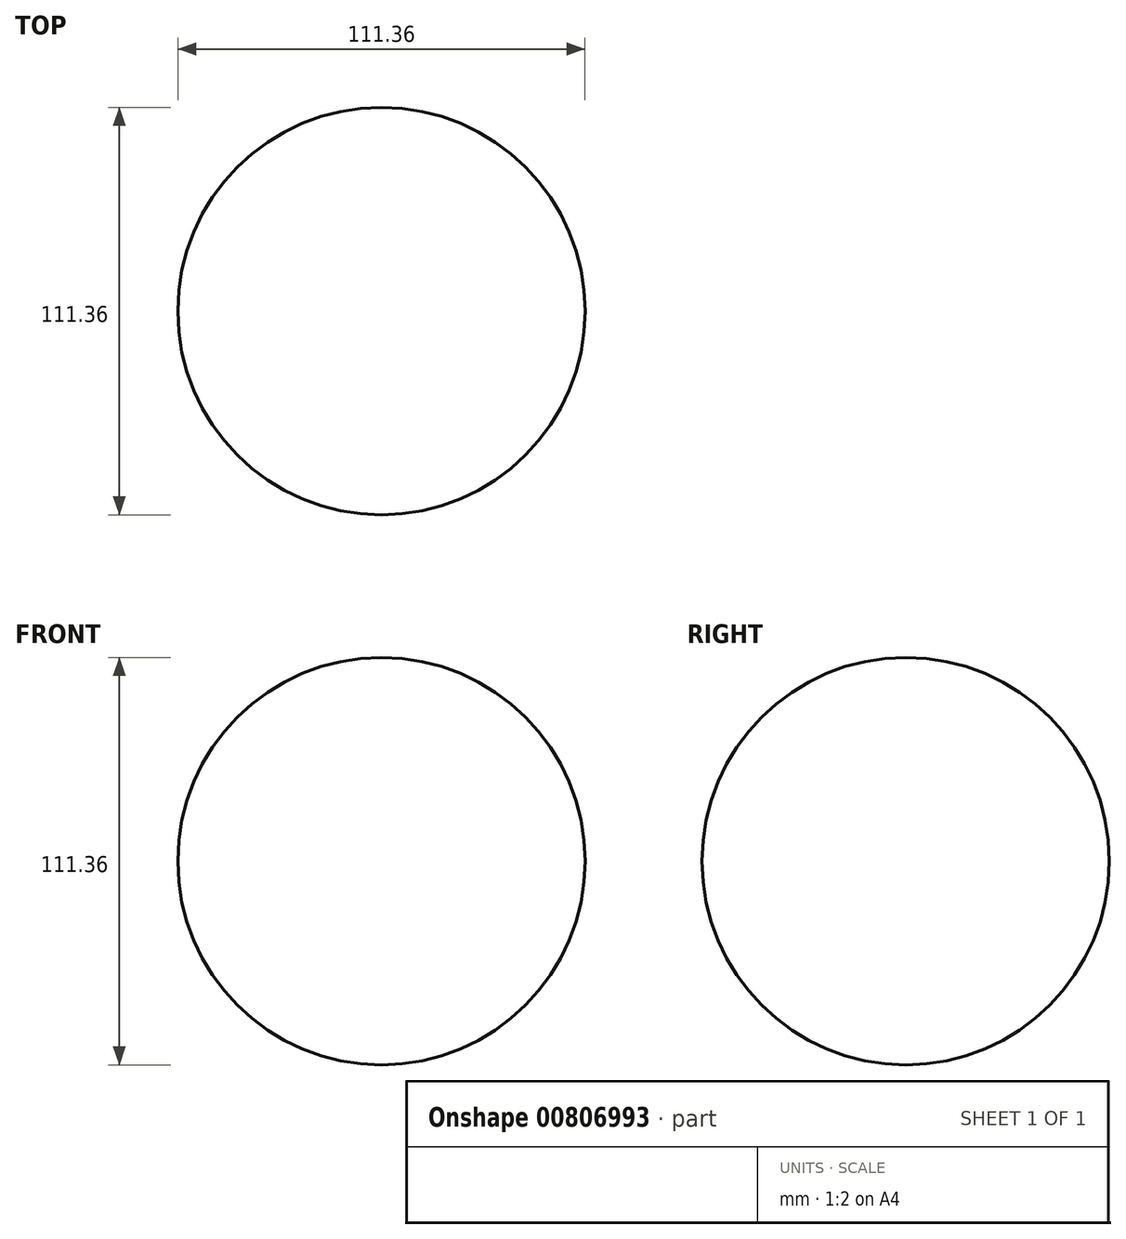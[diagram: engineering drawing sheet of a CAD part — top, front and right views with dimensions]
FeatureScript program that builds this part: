
annotation { "Feature Type Name" : "Feature", "Feature Type Description" : "" }
export const myFeature = defineFeature(function(context is Context, id is Id, definition is map)
    precondition{}
    {
        {
            var Q0;
            Q0=qCreatedBy(makeId("Front.planeOp"),FACE);
            var sketch = newSketch(context, id + "F0", { "sketchPlane" : qUnion([Q0])});
            skCircle(sketch, "E0", {"center": v(0, 0) * mm, "radius": 55.68 * mm});
            skLineSegment(sketch, "E1", {"start": v(0, 0) * mm, "end": v(0, 71.37) * mm});
            skLineSegment(sketch, "E2", {"start": v(0, 71.37) * mm, "end": v(0, -70.76) * mm});
            skSolve(sketch);
        }
        {
            var Q0;
            {var subQ0=sQuery(id+"F0.wireOp",EDGE,"E1");var subQ1=sQuery(id+"F0.wireOp",EDGE,"E0");var subQ2=makeQuery(id+"F0.imprint","INTERSECT",VERTEX,{"derivedFrom":[subQ1,subQ0]});Q0=makeQuery(id+"F0.imprint","IMPRINT",FACE,{"disambiguationData":[TD([[makeQuery(id+"F0.imprint","IMPRINT",EDGE,{"disambiguationData":[TD([[subQ2,-1.0]])],"derivedFrom":subQ1}),1.0]])]});}
            var Q1;
            Q1=sQuery(id+"F0.wireOp",EDGE,"E2");
            revolve(context, id + "F1", {"surfaceOperationType" : NewSurfaceOperationType.NEW, "entities" : qUnion([Q0]), "axis" : qUnion([Q1]), "revolveType" : RevolveType.FULL});
        }
    });
